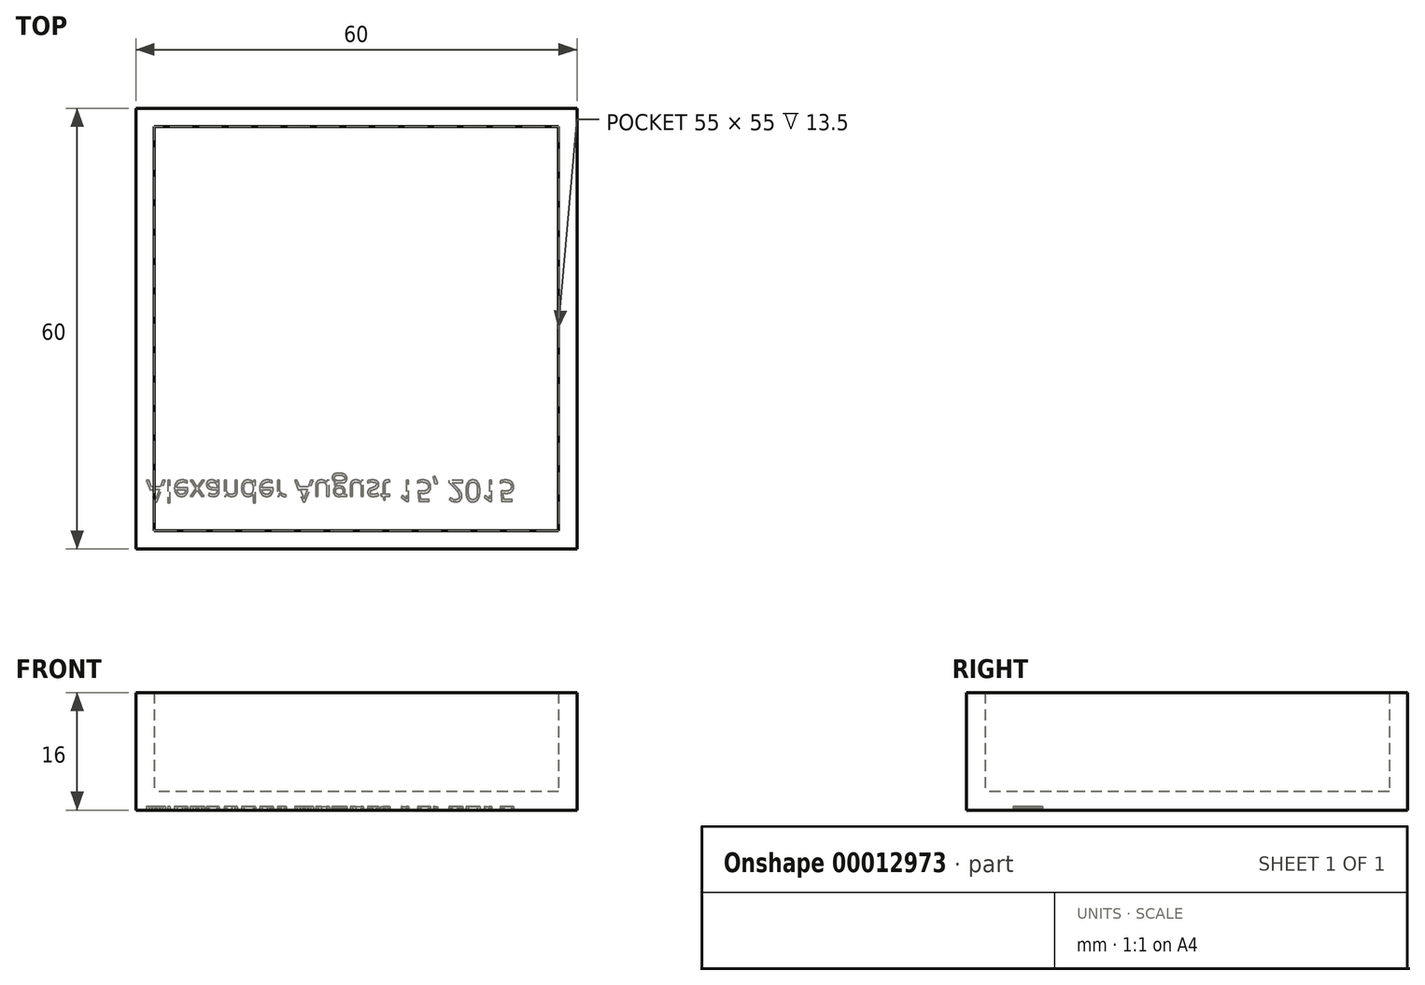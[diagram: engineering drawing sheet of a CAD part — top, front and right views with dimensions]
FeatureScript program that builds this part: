
annotation { "Feature Type Name" : "Feature", "Feature Type Description" : "" }
export const myFeature = defineFeature(function(context is Context, id is Id, definition is map)
    precondition{}
    {
        {
            var Q0;
            Q0=qCreatedBy(makeId("Top.planeOp"),FACE);
            var sketch = newSketch(context, id + "F0", { "sketchPlane" : qUnion([Q0])});
            skLineSegment(sketch, "E0.rect.bottom", {"start": v(30, 30) * mm, "end": v(-30, 30) * mm});
            skLineSegment(sketch, "E0.rect.top", {"start": v(30, -30) * mm, "end": v(-30, -30) * mm});
            skLineSegment(sketch, "E0.rect.left", {"start": v(30, 30) * mm, "end": v(30, -30) * mm});
            skLineSegment(sketch, "E0.rect.right", {"start": v(-30, 30) * mm, "end": v(-30, -30) * mm});
            skPoint(sketch, "E0.rect.middle", {"position": v(0, 0) * mm});
            skSolve(sketch);
        }
        {
            var Q0;
            Q0 = qSketchRegion(id + "F0", true);
            extrude(context, id + "F1", {"entities" : qUnion([Q0]), "depth" : 16 * mm});
        }
        {
            var Q0;
            Q0=makeQuery(id+"F1.opExtrude","CAP_FACE",FACE,{"disambiguationData":[OSD([sQuery(id+"F0.wireOp",EDGE,"E0.rect.bottom"),sQuery(id+"F0.wireOp",EDGE,"E0.rect.top"),sQuery(id+"F0.wireOp",EDGE,"E0.rect.left"),sQuery(id+"F0.wireOp",EDGE,"E0.rect.right")])],"isStart":false});
            shell(context, id + "F2", {"entities" : qUnion([Q0]), "thickness" : 2.5 * mm});
        }
        {
            var Q0;
            Q0=makeQuery(id+"F1.opExtrude","CAP_FACE",FACE,{"disambiguationData":[OSD([sQuery(id+"F0.wireOp",EDGE,"E0.rect.bottom"),sQuery(id+"F0.wireOp",EDGE,"E0.rect.top"),sQuery(id+"F0.wireOp",EDGE,"E0.rect.left"),sQuery(id+"F0.wireOp",EDGE,"E0.rect.right")])],"isStart":true});
            var sketch = newSketch(context, id + "F3", { "sketchPlane" : qUnion([Q0])});
            skText(sketch, "E1", { "text": "Alexander August 15, 2015", "fontName": "OpenSans-Regular.ttf"});
            const initialGuessF3  = {"E1": [-0.02857, 0.02063, 1, 0, 0.00291]};
            skSetInitialGuess(sketch, initialGuessF3);
            skSolve(sketch);
        }
        {
            var Q0;
            Q0 = qSketchRegion(id + "F3", true);
            extrude(context, id + "F4", {"entities" : qUnion([Q0]), "operationType" : NewBodyOperationType.REMOVE, "oppositeDirection" : true, "depth" : 0.5 * mm});
        }
    });
